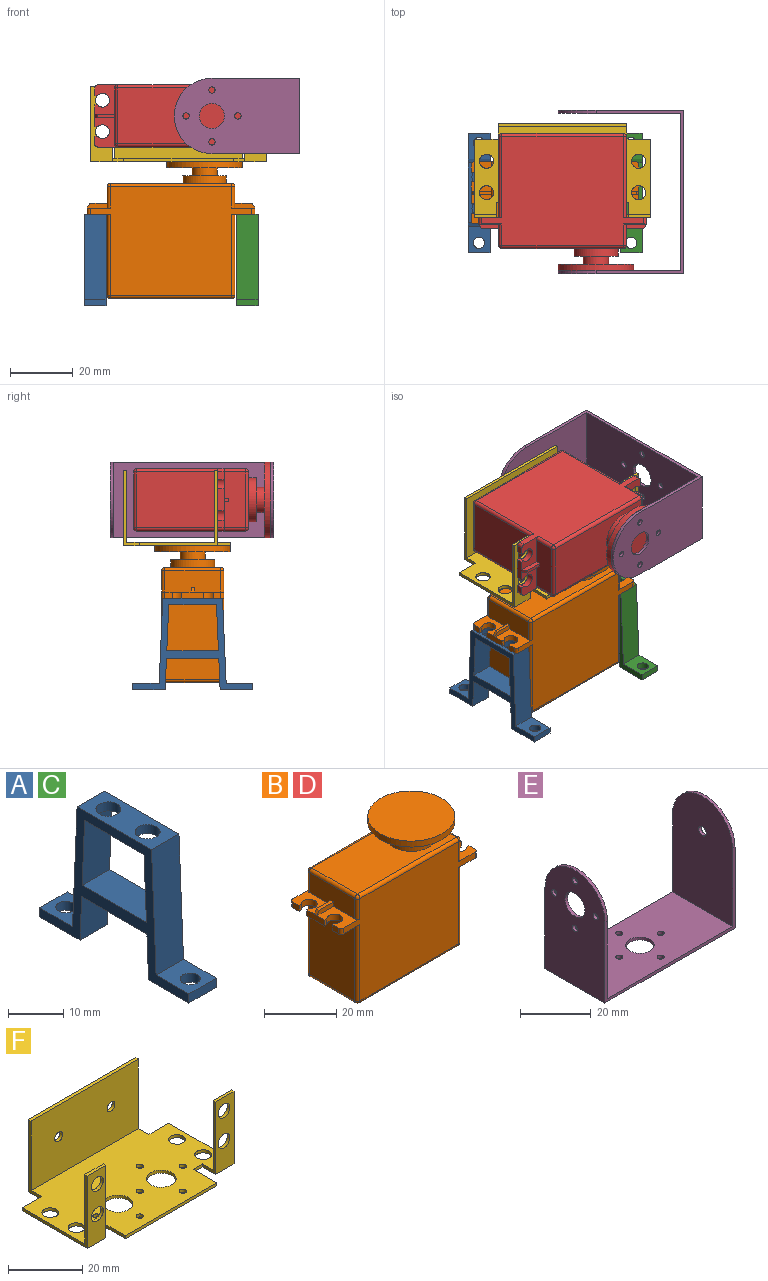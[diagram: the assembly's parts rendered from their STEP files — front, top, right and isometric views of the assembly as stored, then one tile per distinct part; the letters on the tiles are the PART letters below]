
ASSEMBLY  parts=6 mates=5
PART A: 22 faces, bbox 7x38.1x29.1 mm
  f0: plane 9.9x7mm, normal (0,-1,-0.04), area 69.4mm2, adj f1,f11,f12,f13
  f1: plane 10.3x7mm, normal (0,0,-1), area 61.9mm2, adj f0,f2,f12,f13,f21
  f2: plane 7x2mm, normal (0,1,0), area 14mm2, adj f1,f3,f12,f13
  f3: plane 8.38x7mm, normal (0,0,1), area 48.5mm2, adj f2,f4,f12,f13,f21
  f4: plane 27.1x7mm, normal (0,1,0.04), area 189.9mm2, adj f3,f5,f12,f13
  f5: plane 19x7mm, normal (0,0,1), area 101.2mm2, adj f4,f6,f12,f13,f18,f19
  f6: plane 27.1x7mm, normal (0,-1,0.04), area 189.9mm2, adj f5,f7,f12,f13
  f7: plane 8.38x7mm, normal (0,0,1), area 48.5mm2, adj f6,f8,f12,f13,f20
  f8: plane 7x2mm, normal (0,-1,0), area 14mm2, adj f7,f9,f12,f13
  f9: plane 10.3x7mm, normal (0,0,-1), area 61.9mm2, adj f8,f10,f12,f13,f20
  f10: plane 9.9x7mm, normal (0,1,-0.04), area 69.4mm2, adj f9,f11,f12,f13
  f11: plane 16.65x7mm, normal (0,0,-1), area 116.5mm2, adj f0,f10,f12,f13
  f12: plane 38.1x29.1mm, normal (1,0,0), area 221.4mm2, adj f0,f1,f2,f3,f4,f5,f6,f7
  f13: plane 38.1x29.1mm, normal (-1,0,0), area 221.4mm2, adj f0,f1,f2,f3,f4,f5,f6,f7
  f14: plane 14.7x7mm, normal (0,1,-0.04), area 103mm2, adj f12,f13,f15,f17
  f15: plane 16.43x7mm, normal (0,0,1), area 115mm2, adj f12,f13,f14,f16
  f16: plane 14.7x7mm, normal (0,-1,-0.04), area 103mm2, adj f12,f13,f15,f17
  f17: plane 15.17x7mm, normal (0,0,-1), area 74.4mm2, adj f12,f13,f14,f16,f18,f19
  f18: cylinder r=2.25mm len=4.5mm, axis (0,0,1), area 28.3mm2, adj f5,f17
  f19: cylinder r=2.25mm len=4.5mm, axis (0,0,1), area 28.3mm2, adj f5,f17
  f20: cylinder r=1.8mm len=3.6mm, axis (0,0,1), area 22.6mm2, adj f7,f9
  f21: cylinder r=1.8mm len=3.6mm, axis (0,0,1), area 22.6mm2, adj f1,f3
PART B: 74 faces, bbox 53.4x24x43.6 mm
  f0: plane 9.4x7.4mm, normal (0,0,1), area 43.6mm2, adj f1,f4,f8,f13,f35,f36,f37,f51
  f1: plane 17.8x6.8mm, normal (-1,0,0), area 119.5mm2, adj f0,f5,f56,f62,f65,f71,f72,f73
  f2: plane 9.4x7.4mm, normal (0,0,1), area 43.6mm2, adj f3,f9,f12,f22,f26,f27,f28,f52
  f3: plane 17.8x6.8mm, normal (1,0,0), area 119.5mm2, adj f2,f7,f54,f58,f59,f67,f68,f69
  f4: plane 2.4x2mm, normal (-1,0,0), area 4.8mm2, adj f0,f25,f35,f51
  f5: plane 9.4x7.4mm, normal (0,0,1), area 43.6mm2, adj f1,f8,f12,f24,f29,f30,f31,f50
  f6: plane 2.4x2mm, normal (1,0,0), area 4.8mm2, adj f7,f23,f32,f53
  f7: plane 9.4x7.4mm, normal (0,0,1), area 43.6mm2, adj f3,f6,f9,f13,f32,f33,f34,f53
  f8: plane 7x2mm, normal (-1,0,0), area 14mm2, adj f0,f5,f25,f31,f36,f70
  f9: plane 7x2mm, normal (1,0,0), area 14mm2, adj f2,f7,f23,f27,f34,f66
  f10: plane 25.8x17.8mm, normal (-1,0,0), area 459.2mm2, adj f25,f40,f46,f49
  f11: plane 25.8x17.8mm, normal (1,0,0), area 459.2mm2, adj f23,f38,f42,f43
  f12: plane 51.4x34.6mm, normal (0,-1,0), area 1361.2mm2, adj f2,f5,f23,f25,f38,f40,f41,f50
  f13: plane 51.4x34.6mm, normal (0,1,0), area 1361.2mm2, adj f0,f7,f23,f25,f43,f47,f49,f51
  f14: plane 38.6x17.8mm, normal (0,0,1), area 533.1mm2, adj f16,f57,f58,f62,f63
  f15: plane 38.6x17.8mm, normal (0,0,-1), area 687.1mm2, adj f41,f42,f46,f47
  f16: cylinder r=7mm len=14mm, axis (0,0,-1), area 110mm2, adj f14,f17
  f17: plane 14x14mm, normal (0,0,1), area 103.7mm2, adj f16,f18
  f18: cylinder r=4mm len=8mm, axis (0,0,-1), area 62.8mm2, adj f17,f21
  f19: cylinder r=12mm len=24mm, axis (0,0,-1), area 150.8mm2, adj f20,f21
  f20: plane 24x24mm, normal (0,0,1), area 452.4mm2, adj f19
  f21: plane 24x24mm, normal (0,0,-1), area 402.1mm2, adj f18,f19
  f22: plane 2.4x2mm, normal (1,0,0), area 4.8mm2, adj f2,f23,f26,f52
  f23: plane 19.8x7.4mm, normal (0,0,-1), area 93.6mm2, adj f6,f9,f11,f12,f13,f22,f26,f27
  f24: plane 2.4x2mm, normal (-1,0,0), area 4.8mm2, adj f5,f25,f29,f50
  f25: plane 19.8x7.4mm, normal (0,0,-1), area 93.6mm2, adj f4,f8,f10,f12,f13,f24,f29,f30
  f26: plane 2x0.9mm, normal (0,1,0), area 1.8mm2, adj f2,f22,f23,f28
  f27: plane 2x0.9mm, normal (0,-1,0), area 1.8mm2, adj f2,f9,f23,f28
  f28: cylinder r=2.19mm len=4.38mm, axis (0,0,-1), area 20.9mm2, adj f2,f23,f26,f27
  f29: plane 2x0.9mm, normal (0,1,0), area 1.8mm2, adj f5,f24,f25,f30
  f30: cylinder r=2.19mm len=4.38mm, axis (0,0,-1), area 20.9mm2, adj f5,f25,f29,f31
  f31: plane 2x0.9mm, normal (0,-1,0), area 1.8mm2, adj f5,f8,f25,f30
  f32: plane 2x0.9mm, normal (0,-1,0), area 1.8mm2, adj f6,f7,f23,f33
  f33: cylinder r=2.19mm len=4.38mm, axis (0,0,-1), area 20.9mm2, adj f7,f23,f32,f34
  f34: plane 2x0.9mm, normal (0,1,0), area 1.8mm2, adj f7,f9,f23,f33
  f35: plane 2x0.9mm, normal (0,-1,0), area 1.8mm2, adj f0,f4,f25,f37
  f36: plane 2x0.9mm, normal (0,1,0), area 1.8mm2, adj f0,f8,f25,f37
  f37: cylinder r=2.19mm len=4.38mm, axis (0,0,-1), area 20.9mm2, adj f0,f25,f35,f36
  f38: cylinder r=1mm len=25.8mm, axis (0,0,1), area 40.5mm2, adj f11,f12,f23,f39
  f39: sphere r=1mm, area 1.6mm2, adj f38,f41,f42
  f40: cylinder r=1mm len=25.8mm, axis (0,0,-1), area 40.5mm2, adj f10,f12,f25,f44
  f41: cylinder r=1mm len=38.6mm, axis (1,0,0), area 60.6mm2, adj f12,f15,f39,f44
  f42: cylinder r=1mm len=17.8mm, axis (0,1,0), area 28mm2, adj f11,f15,f39,f45
  f43: cylinder r=1mm len=25.8mm, axis (0,0,-1), area 40.5mm2, adj f11,f13,f23,f45
  f44: sphere r=1mm, area 1.6mm2, adj f40,f41,f46
  f45: sphere r=1mm, area 1.6mm2, adj f42,f43,f47
  f46: cylinder r=1mm len=17.8mm, axis (0,-1,0), area 28mm2, adj f10,f15,f44,f48
  f47: cylinder r=1mm len=38.6mm, axis (-1,0,0), area 60.6mm2, adj f13,f15,f45,f48
  f48: sphere r=1mm, area 1.6mm2, adj f46,f47,f49
  f49: cylinder r=1mm len=25.8mm, axis (0,0,1), area 40.5mm2, adj f10,f13,f25,f48
  f50: cylinder r=1mm len=2mm, axis (0,0,-1), area 3.1mm2, adj f5,f12,f24,f25
  f51: cylinder r=1mm len=2mm, axis (0,0,1), area 3.1mm2, adj f0,f4,f13,f25
  f52: cylinder r=1mm len=2mm, axis (0,0,1), area 3.1mm2, adj f2,f12,f22,f23
  f53: cylinder r=1mm len=2mm, axis (0,0,-1), area 3.1mm2, adj f6,f7,f13,f23
  f54: cylinder r=1mm len=6.8mm, axis (0,0,-1), area 10.7mm2, adj f3,f7,f13,f55
  f55: sphere r=1mm, area 1.6mm2, adj f54,f57,f58
  f56: cylinder r=1mm len=6.8mm, axis (0,0,1), area 10.7mm2, adj f0,f1,f13,f60
  f57: cylinder r=1mm len=38.6mm, axis (1,0,0), area 60.6mm2, adj f13,f14,f55,f60
  f58: cylinder r=1mm len=17.8mm, axis (0,-1,0), area 28mm2, adj f3,f14,f55,f61
  f59: cylinder r=1mm len=6.8mm, axis (0,0,1), area 10.7mm2, adj f2,f3,f12,f61
  f60: sphere r=1mm, area 1.6mm2, adj f56,f57,f62
  f61: sphere r=1mm, area 1.6mm2, adj f58,f59,f63
  f62: cylinder r=1mm len=17.8mm, axis (0,1,0), area 28mm2, adj f1,f14,f60,f64
  f63: cylinder r=1mm len=38.6mm, axis (-1,0,0), area 60.6mm2, adj f12,f14,f61,f64
  f64: sphere r=1mm, area 1.6mm2, adj f62,f63,f65
  f65: cylinder r=1mm len=6.8mm, axis (0,0,-1), area 10.7mm2, adj f1,f5,f12,f64
  f66: plane 1.5x1mm, normal (0.87,0,0.5), area 1.7mm2, adj f9,f67,f68,f69
  f67: plane 5.53x1mm, normal (0,0,1), area 5.5mm2, adj f3,f66,f68,f69
  f68: plane 6.4x1.5mm, normal (0,-1,0), area 9mm2, adj f2,f3,f66,f67
  f69: plane 6.4x1.5mm, normal (0,1,0), area 9mm2, adj f3,f7,f66,f67
  f70: plane 1.5x1mm, normal (-0.87,0,0.5), area 1.7mm2, adj f8,f71,f72,f73
  f71: plane 5.53x1mm, normal (0,0,1), area 5.5mm2, adj f1,f70,f72,f73
  f72: plane 6.4x1.5mm, normal (0,-1,0), area 9mm2, adj f1,f5,f70,f71
  f73: plane 6.4x1.5mm, normal (0,1,0), area 9mm2, adj f0,f1,f70,f71
PART C: same geometry as A
PART D: same geometry as B
PART E: 21 faces, bbox 52x24x40 mm
  f0: plane 50x24mm, normal (0,0,1), area 1137.2mm2, adj f1,f3,f7,f9,f10,f11,f12,f13
  f1: plane 52x28mm, normal (0,1,0), area 106mm2, adj f0,f2,f4,f5,f6,f7,f8,f9
  f2: plane 40x24mm, normal (-1,0,0), area 835.4mm2, adj f1,f3,f5,f6,f15,f16,f17,f18
  f3: plane 52x28mm, normal (0,-1,0), area 106mm2, adj f0,f2,f4,f5,f6,f7,f8,f9
  f4: plane 40x24mm, normal (1,0,0), area 891.1mm2, adj f1,f3,f5,f8,f20
  f5: plane 52x24mm, normal (0,0,-1), area 1185.2mm2, adj f1,f2,f3,f4,f10,f11,f12,f13
  f6: cylinder r=12mm len=24mm, axis (-1,0,0), area 37.7mm2, adj f1,f2,f3,f7
  f7: plane 39x24mm, normal (1,0,0), area 811.4mm2, adj f0,f1,f3,f6,f15,f16,f17,f18
  f8: cylinder r=12mm len=24mm, axis (1,0,0), area 37.7mm2, adj f1,f3,f4,f9
  f9: plane 39x24mm, normal (-1,0,0), area 867.1mm2, adj f0,f1,f3,f8,f20
  f10: cylinder r=4mm len=8mm, axis (0,0,1), area 25.1mm2, adj f0,f5
  f11: cylinder r=1mm len=2mm, axis (0,0,1), area 6.3mm2, adj f0,f5
  f12: cylinder r=1mm len=2mm, axis (0,0,1), area 6.3mm2, adj f0,f5
  f13: cylinder r=1mm len=2mm, axis (0,0,1), area 6.3mm2, adj f0,f5
  f14: cylinder r=1mm len=2mm, axis (0,0,1), area 6.3mm2, adj f0,f5
  f15: cylinder r=4mm len=8mm, axis (-1,0,0), area 25.1mm2, adj f2,f7
  f16: cylinder r=1mm len=2mm, axis (-1,0,0), area 6.3mm2, adj f2,f7
  f17: cylinder r=1mm len=2mm, axis (-1,0,0), area 6.3mm2, adj f2,f7
  f18: cylinder r=1mm len=2mm, axis (-1,0,0), area 6.3mm2, adj f2,f7
  f19: cylinder r=1mm len=2mm, axis (-1,0,0), area 6.3mm2, adj f2,f7
  f20: cylinder r=1.5mm len=3mm, axis (1,0,0), area 9.4mm2, adj f4,f9
PART F: 43 faces, bbox 56x34x24 mm
  f0: plane 56x33mm, normal (0,0,1), area 1468.9mm2, adj f1,f2,f3,f4,f5,f7,f8,f9
  f1: plane 9x1mm, normal (-1,0,0), area 9mm2, adj f0,f2,f16,f17
  f2: plane 35x1mm, normal (0,-1,0), area 35mm2, adj f0,f1,f3,f17
  f3: plane 9x1mm, normal (1,0,0), area 9mm2, adj f0,f2,f4,f17
  f4: plane 3.5x1mm, normal (0,-1,0), area 3.5mm2, adj f0,f3,f5,f17
  f5: plane 24x5mm, normal (-1,0,0), area 28mm2, adj f0,f4,f6,f17,f20,f21
  f6: plane 24x7mm, normal (0,-1,0), area 136.2mm2, adj f5,f7,f17,f20,f37,f38
  f7: plane 25x24mm, normal (1,0,0), area 48mm2, adj f0,f6,f8,f17,f20,f21
  f8: plane 7.5x1mm, normal (0,1,0), area 7.5mm2, adj f0,f7,f9,f17
  f9: plane 24x5mm, normal (1,0,0), area 28mm2, adj f0,f8,f10,f17,f18,f19
  f10: plane 41x24mm, normal (0,1,0), area 969.9mm2, adj f9,f11,f17,f18,f41,f42
  f11: plane 24x5mm, normal (-1,0,0), area 28mm2, adj f0,f10,f12,f17,f18,f19
  f12: plane 7.5x1mm, normal (0,1,0), area 7.5mm2, adj f0,f11,f13,f17
  f13: plane 25x24mm, normal (-1,0,0), area 48mm2, adj f0,f12,f14,f17,f22,f23
  f14: plane 24x7mm, normal (0,-1,0), area 136.2mm2, adj f13,f15,f17,f22,f39,f40
  f15: plane 24x5mm, normal (1,0,0), area 28mm2, adj f0,f14,f16,f17,f22,f23
  f16: plane 3.5x1mm, normal (0,-1,0), area 3.5mm2, adj f0,f1,f15,f17
  f17: plane 56x34mm, normal (0,0,-1), area 1523.9mm2, adj f1,f2,f3,f4,f5,f6,f7,f8
  f18: plane 41x1mm, normal (0,0,1), area 41mm2, adj f9,f10,f11,f19
  f19: plane 41x23mm, normal (0,-1,0), area 928.9mm2, adj f0,f9,f11,f18,f41,f42
  f20: plane 7x1mm, normal (0,0,1), area 7mm2, adj f5,f6,f7,f21
  f21: plane 23x7mm, normal (0,1,0), area 129.2mm2, adj f0,f5,f7,f20,f37,f38
  f22: plane 7x1mm, normal (0,0,1), area 7mm2, adj f13,f14,f15,f23
  f23: plane 23x7mm, normal (0,1,0), area 129.2mm2, adj f0,f13,f15,f22,f39,f40
  f24: cylinder r=4mm len=8mm, axis (0,0,1), area 25.1mm2, adj f0,f17
  f25: cylinder r=1mm len=2mm, axis (0,0,1), area 6.3mm2, adj f0,f17
  f26: cylinder r=1mm len=2mm, axis (0,0,1), area 6.3mm2, adj f0,f17
  f27: cylinder r=1mm len=2mm, axis (0,0,1), area 6.3mm2, adj f0,f17
  f28: cylinder r=1mm len=2mm, axis (0,0,1), area 6.3mm2, adj f0,f17
  f29: cylinder r=2.25mm len=4.5mm, axis (0,0,1), area 14.1mm2, adj f0,f17
  f30: cylinder r=2.25mm len=4.5mm, axis (0,0,1), area 14.1mm2, adj f0,f17
  f31: cylinder r=4mm len=8mm, axis (0,0,1), area 25.1mm2, adj f0,f17
  f32: cylinder r=1mm len=2mm, axis (0,0,1), area 6.3mm2, adj f0,f17
  f33: cylinder r=1mm len=2mm, axis (0,0,1), area 6.3mm2, adj f0,f17
  f34: cylinder r=1mm len=2mm, axis (0,0,1), area 6.3mm2, adj f0,f17
  f35: cylinder r=2.25mm len=4.5mm, axis (0,0,1), area 14.1mm2, adj f0,f17
  f36: cylinder r=2.25mm len=4.5mm, axis (0,0,1), area 14.1mm2, adj f0,f17
  f37: cylinder r=2.25mm len=4.5mm, axis (0,-1,0), area 14.1mm2, adj f6,f21
  f38: cylinder r=2.25mm len=4.5mm, axis (0,-1,0), area 14.1mm2, adj f6,f21
  f39: cylinder r=2.25mm len=4.5mm, axis (0,-1,0), area 14.1mm2, adj f14,f23
  f40: cylinder r=2.25mm len=4.5mm, axis (0,-1,0), area 14.1mm2, adj f14,f23
  f41: cylinder r=1.5mm len=3mm, axis (0,1,0), area 9.4mm2, adj f10,f19
  f42: cylinder r=1.5mm len=3mm, axis (0,1,0), area 9.4mm2, adj f10,f19
PLACE A t=(-57.49,6.22,-0.39)mm
PLACE B t=(-29.79,6.22,1.91)mm
PLACE C t=(-9.09,6.22,-0.39)mm fixed
PLACE D rot(axis=(1,0,0),90deg) t=(-27.4,25.02,60.01)mm
PLACE E rot(axis=(-0.58,-0.58,0.58),120deg) t=(11.24,6.42,60.01)mm
PLACE F t=(-27.4,11.22,45.51)mm
MATE revolute B.f16 <-> F.f24  axis (0,0,1) through (-19.15,6.22,45.51)mm
MATE fastened B.f33 <-> C.f18  axis (0,0,-1) through (-5.59,11.22,28.71)mm
MATE revolute E.f6 <-> D.f16  axis (0,1,0) through (-16.76,-18.58,60.01)mm
MATE fastened A.f18 <-> B.f37  axis (0,0,1) through (-53.99,11.22,28.71)mm
MATE fastened D.f33 <-> F.f38  axis (0,1,0) through (-3.2,-1.78,65.01)mm
